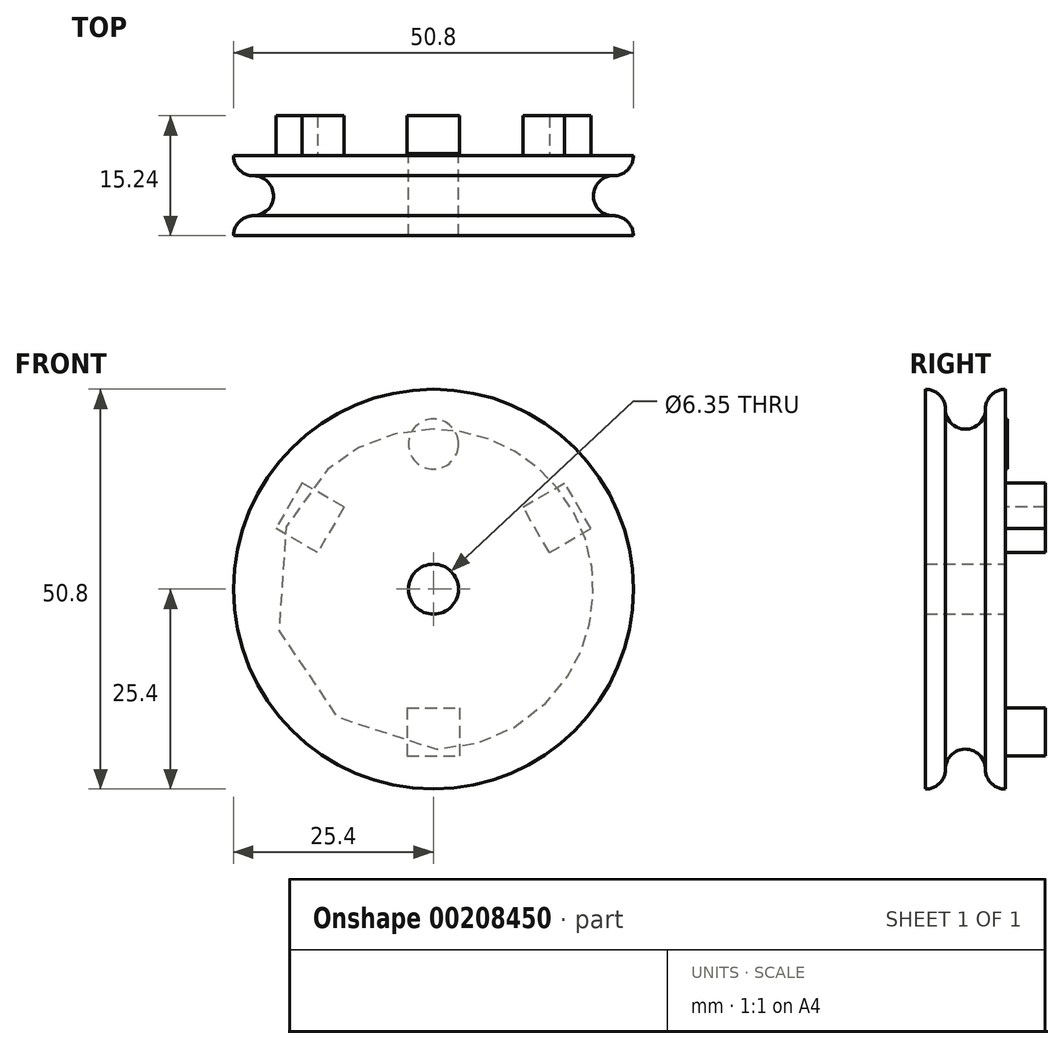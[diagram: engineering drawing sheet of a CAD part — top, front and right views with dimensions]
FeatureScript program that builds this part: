
annotation { "Feature Type Name" : "Feature", "Feature Type Description" : "" }
export const myFeature = defineFeature(function(context is Context, id is Id, definition is map)
    precondition{}
    {
        {
            var Q0;
            Q0=qCreatedBy(makeId("Front.planeOp"),FACE);
            var sketch = newSketch(context, id + "F0", { "sketchPlane" : qUnion([Q0])});
            skCircle(sketch, "E0", {"center": v(0, 0) * mm, "radius": 20.32 * mm});
            skSolve(sketch);
        }
        {
            var Q0;
            Q0=qSketchRegion(id+"F0",true);
            extrude(context, id + "F1", {"entities" : qUnion([Q0]), "endBound" : BoundingType.SYMMETRIC, "depth" : 5.08 * mm});
        }
        {
            var Q0;
            Q0=makeQuery(id+"F1.opExtrude","CAP_FACE",FACE,{"disambiguationData":[OSD([sQuery(id+"F0.wireOp",EDGE,"E0")])],"isStart":false});
            var sketch = newSketch(context, id + "F2", { "sketchPlane" : qUnion([Q0])});
            skCircle(sketch, "E1", {"center": v(0, 0) * mm, "radius": 25.4 * mm});
            skSolve(sketch);
        }
        {
            var Q0;
            Q0=qSketchRegion(id+"F2",true);
            extrude(context, id + "F3", {"entities" : qUnion([Q0]), "operationType" : NewBodyOperationType.ADD, "depth" : 2.54 * mm});
        }
        {
            var Q0;
            Q0=makeQuery(id+"F1.opExtrude","CAP_FACE",FACE,{"disambiguationData":[OSD([sQuery(id+"F0.wireOp",EDGE,"E0")])],"isStart":true});
            var sketch = newSketch(context, id + "F4", { "sketchPlane" : qUnion([Q0])});
            skCircle(sketch, "E2", {"center": v(0, 0) * mm, "radius": 25.4 * mm});
            skSolve(sketch);
        }
        {
            var Q0;
            Q0=qSketchRegion(id+"F4",true);
            extrude(context, id + "F5", {"entities" : qUnion([Q0]), "operationType" : NewBodyOperationType.ADD, "depth" : 2.54 * mm});
        }
        {
            var Q0;
            Q0=makeQuery(id+"F1.opExtrude","SWEPT_FACE",FACE,{"disambiguationData":[OSD([sQuery(id+"F0.wireOp",EDGE,"E0")])]});
            var Q1;
            Q1=makeQuery(id+"F5.opExtrude","CAP_EDGE",EDGE,{"disambiguationData":[OSD([sQuery(id+"F4.wireOp",EDGE,"E2")])],"isStart":true});
            var Q2;
            Q2=makeQuery(id+"F3.opExtrude","CAP_EDGE",EDGE,{"disambiguationData":[OSD([sQuery(id+"F2.wireOp",EDGE,"E1")])],"isStart":true});
            fillet(context, id + "F6", {"entities" : qUnion([Q0, Q1, Q2]), "radius" : 2.54 * mm, "tangentPropagation" : true, "allowEdgeOverflow" : false});
        }
        {
            var Q0;
            Q0=makeQuery(id+"F5.opExtrude","CAP_FACE",FACE,{"disambiguationData":[OSD([sQuery(id+"F4.wireOp",EDGE,"E2")])],"isStart":false});
            var sketch = newSketch(context, id + "F7", { "sketchPlane" : qUnion([Q0])});
            skCircle(sketch, "E3", {"center": v(0, 0) * mm, "radius": 3.18 * mm});
            skCircle(sketch, "E4", {"center": v(0, 18.44) * mm, "radius": 3.18 * mm});
            skSolve(sketch);
        }
        {
            var Q0;
            Q0=makeQuery(id+"F7.imprint","IMPRINT",FACE,{"disambiguationData":[TD([[makeQuery(id+"F7.imprint","IMPRINT",EDGE,{"derivedFrom":sQuery(id+"F7.wireOp",EDGE,"E3")}),1.0]])]});
            extrude(context, id + "F8", {"entities" : qUnion([Q0]), "operationType" : NewBodyOperationType.REMOVE, "oppositeDirection" : true, "depth" : 25.4 * mm});
        }
        {
            var Q0;
            Q0=makeQuery(id+"F7.imprint","IMPRINT",FACE,{"disambiguationData":[TD([[makeQuery(id+"F7.imprint","IMPRINT",EDGE,{"derivedFrom":sQuery(id+"F7.wireOp",EDGE,"E4")}),1.0]])]});
            extrude(context, id + "F9", {"entities" : qUnion([Q0]), "operationType" : NewBodyOperationType.ADD, "depth" : 0.25 * mm});
        }
        {
            var Q0;
            Q0=makeQuery(id+"F5.opExtrude","CAP_FACE",FACE,{"disambiguationData":[OSD([sQuery(id+"F4.wireOp",EDGE,"E2")])],"isStart":false});
            var sketch = newSketch(context, id + "F10", { "sketchPlane" : qUnion([Q0])});
            skLineSegment(sketch, "E5.bottom", {"start": v(3.34, -15.07) * mm, "end": v(-3.34, -15.07) * mm});
            skLineSegment(sketch, "E5.top", {"start": v(3.34, -21.18) * mm, "end": v(-3.34, -21.18) * mm});
            skLineSegment(sketch, "E5.left", {"start": v(3.34, -15.07) * mm, "end": v(3.34, -21.18) * mm});
            skLineSegment(sketch, "E5.right", {"start": v(-3.34, -15.07) * mm, "end": v(-3.34, -21.18) * mm});
            skPoint(sketch, "E5.middle", {"position": v(0, -18.13) * mm});
            skLineSegment(sketch, "E6.1.0", {"start": v(16.68, 13.48) * mm, "end": v(20.02, 7.7) * mm});
            skLineSegment(sketch, "E6.1.1", {"start": v(11.38, 10.42) * mm, "end": v(14.72, 4.64) * mm});
            skPoint(sketch, "E6.1.2", {"position": v(15.7, 9.06) * mm});
            skLineSegment(sketch, "E6.1.3", {"start": v(14.72, 4.64) * mm, "end": v(20.02, 7.7) * mm});
            skLineSegment(sketch, "E6.1.4", {"start": v(11.38, 10.42) * mm, "end": v(16.68, 13.48) * mm});
            skLineSegment(sketch, "E6.2.0", {"start": v(-20.02, 7.7) * mm, "end": v(-16.68, 13.48) * mm});
            skLineSegment(sketch, "E6.2.1", {"start": v(-14.72, 4.64) * mm, "end": v(-11.38, 10.42) * mm});
            skPoint(sketch, "E6.2.2", {"position": v(-15.7, 9.06) * mm});
            skLineSegment(sketch, "E6.2.3", {"start": v(-11.38, 10.42) * mm, "end": v(-16.68, 13.48) * mm});
            skLineSegment(sketch, "E6.2.4", {"start": v(-14.72, 4.64) * mm, "end": v(-20.02, 7.7) * mm});
            skPoint(sketch, "E6.center", {"position": v(0, 0) * mm});
            skSolve(sketch);
        }
        {
            var Q0;
            Q0=makeQuery(id+"F10.imprint","IMPRINT",FACE,{"disambiguationData":[TD([[makeQuery(id+"F10.imprint","IMPRINT",EDGE,{"derivedFrom":sQuery(id+"F10.wireOp",EDGE,"E6.1.0")}),-1.0]])]});
            var Q1;
            Q1=makeQuery(id+"F10.imprint","IMPRINT",FACE,{"disambiguationData":[TD([[makeQuery(id+"F10.imprint","IMPRINT",EDGE,{"derivedFrom":sQuery(id+"F10.wireOp",EDGE,"E5.bottom")}),1.0]])]});
            var Q2;
            Q2=makeQuery(id+"F10.imprint","IMPRINT",FACE,{"disambiguationData":[TD([[makeQuery(id+"F10.imprint","IMPRINT",EDGE,{"derivedFrom":sQuery(id+"F10.wireOp",EDGE,"E6.2.0")}),-1.0]])]});
            extrude(context, id + "F11", {"entities" : qUnion([Q0, Q1, Q2]), "depth" : 5.08 * mm});
        }
    });
